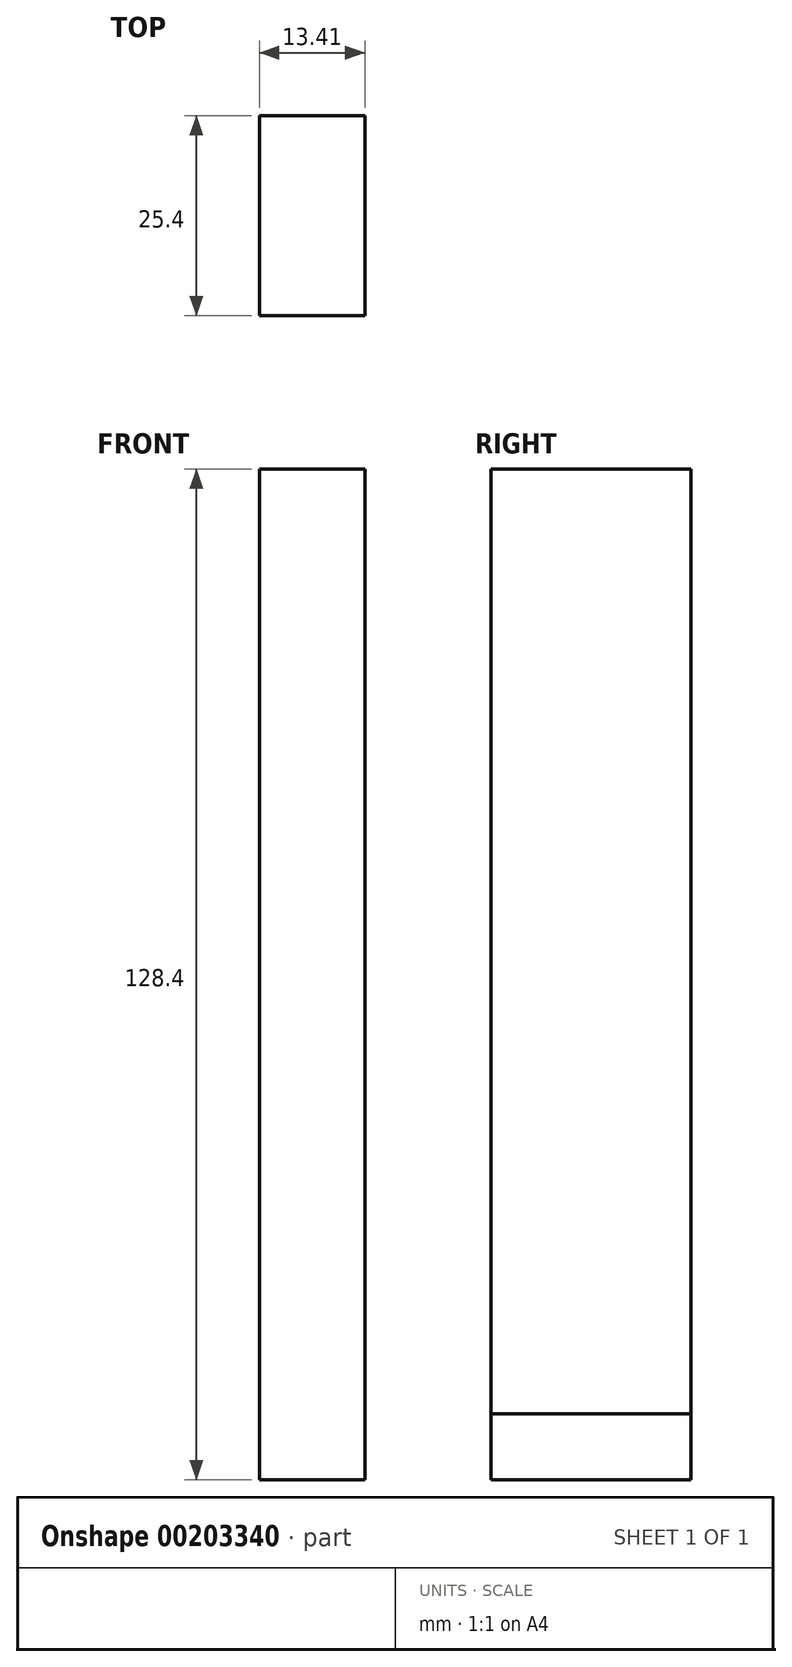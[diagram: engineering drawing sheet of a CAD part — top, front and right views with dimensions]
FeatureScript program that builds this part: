
annotation { "Feature Type Name" : "Feature", "Feature Type Description" : "" }
export const myFeature = defineFeature(function(context is Context, id is Id, definition is map)
    precondition{}
    {
        {
            var Q0;
            Q0=qCreatedBy(makeId("Front.planeOp"),FACE);
            var sketch = newSketch(context, id + "F0", { "sketchPlane" : qUnion([Q0])});
            skLineSegment(sketch, "E0.bottom", {"start": v(-63.26, 62.42) * mm, "end": v(-49.85, 62.42) * mm});
            skLineSegment(sketch, "E0.top", {"start": v(-63.26, -65.98) * mm, "end": v(-49.85, -65.98) * mm});
            skLineSegment(sketch, "E0.left", {"start": v(-63.26, 62.42) * mm, "end": v(-63.26, -65.98) * mm});
            skLineSegment(sketch, "E0.right", {"start": v(-49.85, 62.42) * mm, "end": v(-49.85, -65.98) * mm});
            skLineSegment(sketch, "E1.bottom", {"start": v(38.79, 61.82) * mm, "end": v(46.81, 61.82) * mm});
            skLineSegment(sketch, "E1.top", {"start": v(38.79, -66.58) * mm, "end": v(46.81, -66.58) * mm});
            skLineSegment(sketch, "E1.left", {"start": v(38.79, 61.82) * mm, "end": v(38.79, -66.58) * mm});
            skLineSegment(sketch, "E1.right", {"start": v(46.81, 61.82) * mm, "end": v(46.81, -66.58) * mm});
            skLineSegment(sketch, "E2.bottom", {"start": v(-45.77, 61.92) * mm, "end": v(21.7, 61.92) * mm});
            skLineSegment(sketch, "E2.top", {"start": v(-45.77, 53.8) * mm, "end": v(21.7, 53.8) * mm});
            skLineSegment(sketch, "E2.left", {"start": v(-45.77, 61.92) * mm, "end": v(-45.77, 53.8) * mm});
            skLineSegment(sketch, "E2.right", {"start": v(21.7, 61.92) * mm, "end": v(21.7, 53.8) * mm});
            skLineSegment(sketch, "E3.bottom", {"start": v(-49.85, -57.62) * mm, "end": v(17.62, -57.62) * mm});
            skLineSegment(sketch, "E3.top", {"start": v(-49.85, -65.94) * mm, "end": v(17.62, -65.94) * mm});
            skLineSegment(sketch, "E3.left", {"start": v(-49.85, -57.62) * mm, "end": v(-49.85, -65.94) * mm});
            skLineSegment(sketch, "E3.right", {"start": v(17.62, -57.62) * mm, "end": v(17.62, -65.94) * mm});
            skSolve(sketch);
        }
        {
            var Q0;
            {var subQ1=sQuery(id+"F0.wireOp",EDGE,"E0.bottom");Q0=makeQuery(id+"F0.imprint","IMPRINT",FACE,{"disambiguationData":[TD([[makeQuery(id+"F0.imprint","IMPRINT",EDGE,{"derivedFrom":subQ1}),-1.0]])]});}
            extrude(context, id + "F1", {"entities" : qUnion([Q0]), "endBound" : BoundingType.SYMMETRIC, "depth" : 25.4 * mm});
        }
    });
